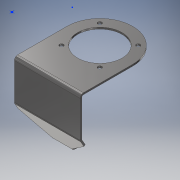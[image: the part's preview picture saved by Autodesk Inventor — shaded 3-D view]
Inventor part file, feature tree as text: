
AUTODESK INVENTOR PART (.ipt)
format: ipt  version: 2018 (Build 220112000, 112)  size: 198,656 bytes
history: native  units: mm
features: other x21, sketch x7, reference x5, hole x2
ambient origin geometry x8: Origin, YZ Plane, XZ Plane, XY Plane, X Axis, Y Axis, Z Axis, Center Point
bodies: Body1 (feature_tree)
feature tree (35):
  other  "Faccia2"
  other  "Flangia1"
  other  "Flangia2"
  hole  "Foro1"  [1 undecoded]
  other  "Flangia4"
  other  "Arrotondamento angolo1"
  hole  "Foro2"  [1 undecoded]
  sketch  "Schizzo1"
  other  "Piano2"
  sketch  "Schizzo2"
  other  "Piano3"
  other  "Piega (Bend)1"
  other  "Angolo1"
  sketch  "Schizzo3"
  other  "Piano4"
  other  "Piega (Bend)2"
  other  "Angolo2"
  sketch  "Schizzo5"
  reference  "Riferimento1"
  reference  "Riferimento2"
  reference  "Riferimento3"
  reference  "Riferimento4"
  sketch  "Schizzo6"
  sketch  "Schizzo7"
  other  "Piano6"
  other  "Piega (Bend)4"
  other  "Angolo4"
  sketch  "Schizzo8"
  reference  "Riferimento5"
  other  "Taglia1"
  other  "Trasmissione cinghie - Taglio.iam"
  other  "Motorredutor Bonfiglioli :1"
  other  "MOTOR_C80_B5_X_X:1"
  other  "Telaietto trasmissione:1"
  other  "Tubolare telaietto corto:12"
note: 2 required parameter values undecoded (feature->parameter linkage not recoverable at this tier; creation-order binding heuristic only, values carry confidence <= 0.55)
